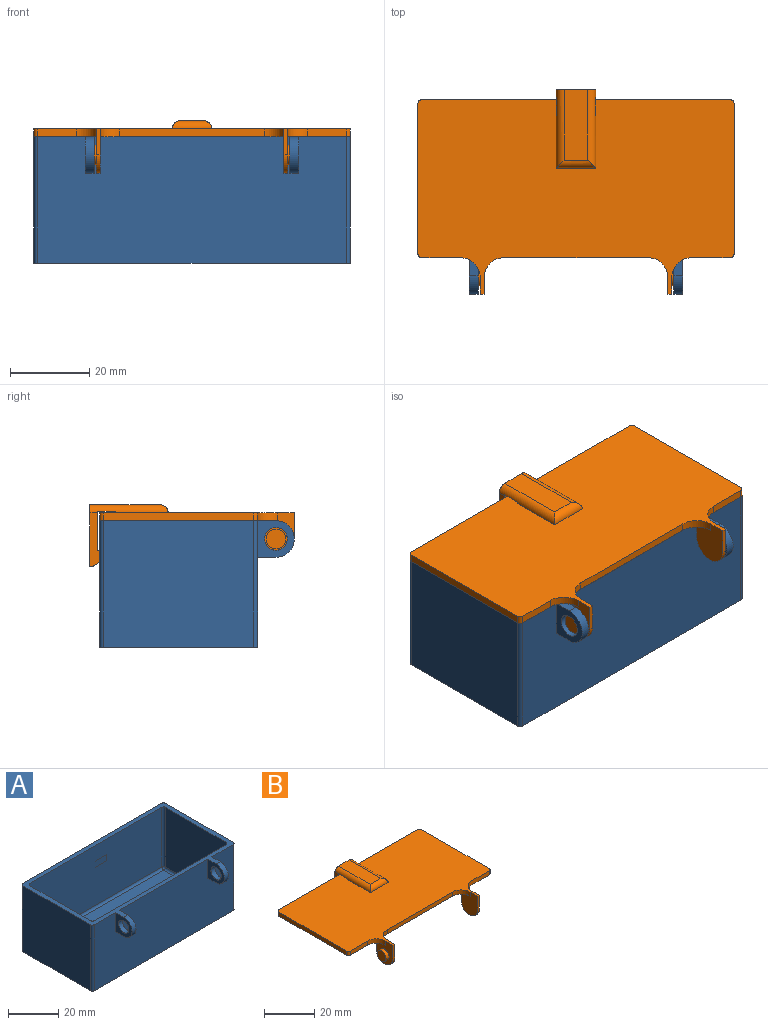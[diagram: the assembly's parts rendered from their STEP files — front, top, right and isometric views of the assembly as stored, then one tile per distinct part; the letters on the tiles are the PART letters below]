
ASSEMBLY  parts=2 mates=1
PART A: 42 faces, bbox 80x49.3x32 mm
  f0: plane 78x32mm, normal (0,1,0), area 2460mm2, adj f4,f9,f35,f36,f37,f38,f39,f40
  f1: plane 38x32mm, normal (-1,0,0), area 1216mm2, adj f4,f9,f33,f36
  f2: plane 78x32mm, normal (0,-1,0), area 2454.4mm2, adj f4,f9,f11,f12,f13,f14,f15,f16
  f3: plane 38x32mm, normal (1,0,0), area 1216mm2, adj f4,f9,f34,f35
  f4: plane 80x40mm, normal (0,0,-1), area 3199.1mm2, adj f0,f1,f2,f3,f33,f34,f35,f36
  f5: plane 74x29mm, normal (0,1,0), area 2146mm2, adj f9,f26,f30,f32
  f6: plane 34x29mm, normal (1,0,0), area 986mm2, adj f9,f23,f29,f32
  f7: plane 74x29mm, normal (0,-1,0), area 2146mm2, adj f9,f21,f23,f24
  f8: plane 34x29mm, normal (-1,0,0), area 986mm2, adj f9,f21,f25,f26
  f9: plane 80x44.63mm, normal (0,0,1), area 484.8mm2, adj f0,f1,f2,f3,f5,f6,f7,f8
  f10: plane 74x34mm, normal (0,0,1), area 2516mm2, adj f24,f25,f29,f30
  f11: plane 9.25x9.25mm, normal (-1,0,0), area 50.4mm2, adj f2,f9,f12,f18,f20
  f12: plane 4.63x2.25mm, normal (0,0,-1), area 10.4mm2, adj f2,f11,f13,f18
  f13: plane 9.25x9.25mm, normal (1,0,0), area 50.4mm2, adj f2,f9,f12,f18,f20
  f14: plane 9.25x9.25mm, normal (-1,0,0), area 50.4mm2, adj f2,f9,f15,f17,f19
  f15: plane 4.63x2.25mm, normal (0,0,-1), area 10.4mm2, adj f2,f14,f16,f17
  f16: plane 9.25x9.25mm, normal (1,0,0), area 50.4mm2, adj f2,f9,f15,f17,f19
  f17: cylinder r=4.62mm len=9.25mm, axis (1,0,0), area 32.7mm2, adj f9,f14,f15,f16
  f18: cylinder r=4.62mm len=9.25mm, axis (1,0,0), area 32.7mm2, adj f9,f11,f12,f13
  f19: cylinder r=2.88mm len=5.75mm, axis (-1,0,0), area 40.6mm2, adj f14,f16
  f20: cylinder r=2.88mm len=5.75mm, axis (-1,0,0), area 40.6mm2, adj f11,f13
  f21: cylinder r=1mm len=29mm, axis (0,0,-1), area 45.6mm2, adj f7,f8,f9,f22
  f22: sphere r=1mm, area 1.6mm2, adj f21,f24,f25
  f23: cylinder r=1mm len=29mm, axis (0,0,1), area 45.6mm2, adj f6,f7,f9,f27
  f24: cylinder r=1mm len=74mm, axis (1,0,0), area 116.2mm2, adj f7,f10,f22,f27
  f25: cylinder r=1mm len=34mm, axis (0,-1,0), area 53.4mm2, adj f8,f10,f22,f28
  f26: cylinder r=1mm len=29mm, axis (0,0,1), area 45.6mm2, adj f5,f8,f9,f28
  f27: sphere r=1mm, area 1.6mm2, adj f23,f24,f29
  f28: sphere r=1mm, area 1.6mm2, adj f25,f26,f30
  f29: cylinder r=1mm len=34mm, axis (0,1,0), area 53.4mm2, adj f6,f10,f27,f31
  f30: cylinder r=1mm len=74mm, axis (-1,0,0), area 116.2mm2, adj f5,f10,f28,f31
  f31: sphere r=1mm, area 1.6mm2, adj f29,f30,f32
  f32: cylinder r=1mm len=29mm, axis (0,0,-1), area 45.6mm2, adj f5,f6,f9,f31
  f33: cylinder r=1mm len=32mm, axis (0,0,1), area 50.3mm2, adj f1,f2,f4,f9
  f34: cylinder r=1mm len=32mm, axis (0,0,-1), area 50.3mm2, adj f2,f3,f4,f9
  f35: cylinder r=1mm len=32mm, axis (0,0,1), area 50.3mm2, adj f0,f3,f4,f9
  f36: cylinder r=1mm len=32mm, axis (0,0,-1), area 50.3mm2, adj f0,f1,f4,f9
  f37: plane 3x1.8mm, normal (-1,0,0), area 5.4mm2, adj f0,f38,f40,f41
  f38: plane 12x1.8mm, normal (0,0,1), area 21.6mm2, adj f0,f37,f39,f41
  f39: plane 3x1.8mm, normal (1,0,0), area 5.4mm2, adj f0,f38,f40,f41
  f40: plane 12x1.8mm, normal (0,0,-1), area 21.6mm2, adj f0,f37,f39,f41
  f41: plane 12x3mm, normal (0,1,0), area 36mm2, adj f37,f38,f39,f40
PART B: 46 faces, bbox 80x51.8x15.7 mm
  f0: plane 9.94x4.5mm, normal (0,0,-1), area 44.7mm2, adj f1,f36,f43,f44
  f1: plane 10x0.35mm, normal (0,1,0), area 3.5mm2, adj f0,f2,f43,f44
  f2: plane 80x49.25mm, normal (0,0,1), area 3105.9mm2, adj f1,f4,f5,f6,f7,f8,f9,f10
  f3: plane 80x45mm, normal (0,0,-1), area 3220.6mm2, adj f4,f5,f7,f8,f9,f11,f12,f13
  f4: plane 9.75x2mm, normal (0,-1,0), area 19.5mm2, adj f2,f3,f22,f29
  f5: plane 11.25x9.25mm, normal (-1,0,0), area 65.2mm2, adj f2,f3,f6,f17,f19,f20,f22
  f6: plane 6.63x1mm, normal (0,-1,0), area 6.6mm2, adj f2,f5,f7,f19
  f7: plane 11.25x9.25mm, normal (1,0,0), area 84.9mm2, adj f2,f3,f6,f17,f19,f23
  f8: plane 36.5x2mm, normal (0,-1,0), area 73mm2, adj f2,f3,f23,f24
  f9: plane 11.25x9.25mm, normal (-1,0,0), area 84.9mm2, adj f2,f3,f10,f16,f18,f24
  f10: plane 6.63x1mm, normal (0,-1,0), area 6.6mm2, adj f2,f9,f11,f18
  f11: plane 11.25x9.25mm, normal (1,0,0), area 65.2mm2, adj f2,f3,f10,f16,f18,f25,f30
  f12: plane 9.75x2mm, normal (0,-1,0), area 19.5mm2, adj f2,f3,f25,f26
  f13: plane 38x2mm, normal (1,0,0), area 76mm2, adj f2,f3,f26,f27
  f14: plane 78x2mm, normal (0,1,0), area 156mm2, adj f2,f3,f27,f28
  f15: plane 38x2mm, normal (-1,0,0), area 76mm2, adj f2,f3,f28,f29
  f16: plane 4.63x1mm, normal (0,1,0), area 4.6mm2, adj f3,f9,f11,f18
  f17: plane 4.63x1mm, normal (0,1,0), area 4.6mm2, adj f3,f5,f7,f19
  f18: cylinder r=4.62mm len=9.25mm, axis (-1,0,0), area 14.5mm2, adj f9,f10,f11,f16
  f19: cylinder r=4.62mm len=9.25mm, axis (-1,0,0), area 14.5mm2, adj f5,f6,f7,f17
  f20: cylinder r=2.5mm len=5mm, axis (1,0,0), area 27.5mm2, adj f5,f21
  f21: plane 5x5mm, normal (-1,0,0), area 19.6mm2, adj f20
  f22: cylinder r=5mm len=5mm, axis (0,0,1), area 15.7mm2, adj f2,f3,f4,f5
  f23: cylinder r=5mm len=5mm, axis (0,0,-1), area 15.7mm2, adj f2,f3,f7,f8
  f24: cylinder r=5mm len=5mm, axis (0,0,1), area 15.7mm2, adj f2,f3,f8,f9
  f25: cylinder r=5mm len=5mm, axis (0,0,-1), area 15.7mm2, adj f2,f3,f11,f12
  f26: cylinder r=1mm len=2mm, axis (0,0,-1), area 3.1mm2, adj f2,f3,f12,f13
  f27: cylinder r=1mm len=2mm, axis (0,0,1), area 3.1mm2, adj f2,f3,f13,f14
  f28: cylinder r=1mm len=2mm, axis (0,0,-1), area 3.1mm2, adj f2,f3,f14,f15
  f29: cylinder r=1mm len=2mm, axis (0,0,1), area 3.1mm2, adj f2,f3,f4,f15
  f30: cylinder r=2.5mm len=5mm, axis (-1,0,0), area 27.5mm2, adj f11,f31
  f31: plane 5x5mm, normal (1,0,0), area 19.6mm2, adj f30
  f32: plane 13.65x4.5mm, normal (-1,0,0), area 31.1mm2, adj f35,f36,f37,f38,f39,f40,f41,f42
  f33: plane 13.65x4.5mm, normal (1,0,0), area 31.1mm2, adj f35,f36,f37,f38,f39,f40,f41,f42
  f34: plane 17.82x6mm, normal (0,0,1), area 106.9mm2, adj f35,f43,f44,f45
  f35: plane 15.65x10mm, normal (0,1,0), area 154.8mm2, adj f32,f33,f34,f37,f43,f44
  f36: plane 10x10mm, normal (0,-1,0), area 100mm2, adj f0,f32,f33,f38,f43,f44
  f37: plane 10x0.17mm, normal (0,0,-1), area 1.7mm2, adj f32,f33,f35,f42
  f38: plane 10x2.5mm, normal (0,0,1), area 25mm2, adj f32,f33,f36,f39
  f39: plane 10x0.09mm, normal (0,-1,0), area 0.9mm2, adj f32,f33,f38,f41
  f40: plane 10x2.62mm, normal (0,-0.71,-0.71), area 37.1mm2, adj f32,f33,f41,f42
  f41: cylinder r=1mm len=10mm, axis (-1,0,0), area 7.9mm2, adj f32,f33,f39,f40
  f42: cylinder r=2mm len=10mm, axis (1,0,0), area 15.7mm2, adj f32,f33,f37,f40
  f43: cylinder r=2mm len=19.82mm, axis (0,1,0), area 58.4mm2, adj f0,f1,f2,f32,f34,f35,f36,f45
  f44: cylinder r=2mm len=19.82mm, axis (0,-1,0), area 58.4mm2, adj f0,f1,f2,f33,f34,f35,f36,f45
  f45: cylinder r=2mm len=10mm, axis (-1,0,0), area 26.8mm2, adj f2,f34,f43,f44
PLACE A rot(axis=(1,0,0),0deg) t=(-36.61,-30.32,-9.05)mm
PLACE B rot(axis=(0.39,-0.56,-0.73),0deg) t=(-40.37,-24.54,22.95)mm
MATE revolute B.f20 <-> A.f17  axis (1,0,0) through (-53.26,-46.81,18.33)mm
